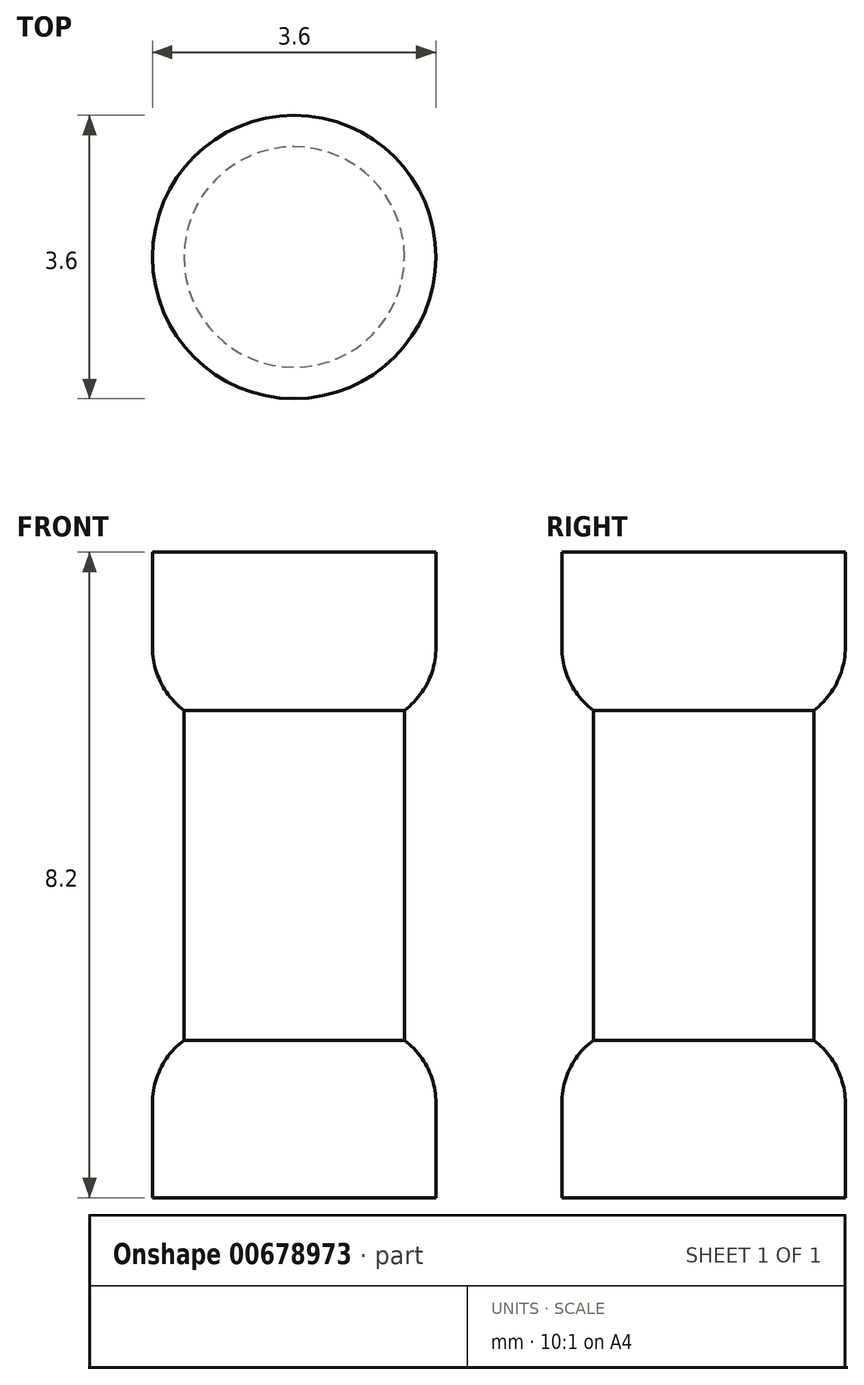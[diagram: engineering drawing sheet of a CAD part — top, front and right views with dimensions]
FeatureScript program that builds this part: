
annotation { "Feature Type Name" : "Feature", "Feature Type Description" : "" }
export const myFeature = defineFeature(function(context is Context, id is Id, definition is map)
    precondition{}
    {
        {
            var Q0;
            Q0=qCreatedBy(makeId("Right.planeOp"),FACE);
            var sketch = newSketch(context, id + "F0", { "sketchPlane" : qUnion([Q0])});
            skLineSegment(sketch, "E0", {"start": v(0, 0) * mm, "end": v(0, 8.2) * mm});
            skLineSegment(sketch, "E1", {"start": v(0, 8.2) * mm, "end": v(-1.8, 8.2) * mm});
            skLineSegment(sketch, "E2", {"start": v(-1.8, 8.2) * mm, "end": v(-1.8, 6.2) * mm});
            skLineSegment(sketch, "E3", {"start": v(0, 0) * mm, "end": v(-1.8, 0) * mm});
            skLineSegment(sketch, "E4", {"start": v(-1.8, 0) * mm, "end": v(-1.8, 2) * mm});
            skLineSegment(sketch, "E5", {"start": v(-1.8, 2) * mm, "end": v(-1.4, 2) * mm});
            skLineSegment(sketch, "E6", {"start": v(-1.4, 2) * mm, "end": v(-1.4, 6.2) * mm});
            skLineSegment(sketch, "E7", {"start": v(-1.4, 6.2) * mm, "end": v(-1.8, 6.2) * mm});
            skSolve(sketch);
        }
        {
            var Q0;
            Q0=makeQuery(id+"F0.imprint","IMPRINT",FACE,{"disambiguationData":[TD([[makeQuery(id+"F0.imprint","IMPRINT",EDGE,{"derivedFrom":sQuery(id+"F0.wireOp",EDGE,"E0")}),1.0]])]});
            var Q1;
            Q1=sQuery(id+"F0.wireOp",EDGE,"E0");
            revolve(context, id + "F1", {"entities" : qUnion([Q0]), "axis" : qUnion([Q1]), "revolveType" : RevolveType.FULL});
        }
        {
            var Q0;
            Q0=makeQuery(id+"F1.opRevolve","SWEPT_EDGE",EDGE,{"disambiguationData":[OSD([sQuery(id+"F0.wireOp",EDGE,"E2"),sQuery(id+"F0.wireOp",EDGE,"E7")])]});
            var Q1;
            Q1=makeQuery(id+"F1.opRevolve","SWEPT_EDGE",EDGE,{"disambiguationData":[OSD([sQuery(id+"F0.wireOp",EDGE,"E4"),sQuery(id+"F0.wireOp",EDGE,"E5")])]});
            fillet(context, id + "F2", {"entities" : qUnion([Q0, Q1]), "radius" : 1 * mm, "tangentPropagation" : true, "allowEdgeOverflow" : false});
        }
    });
